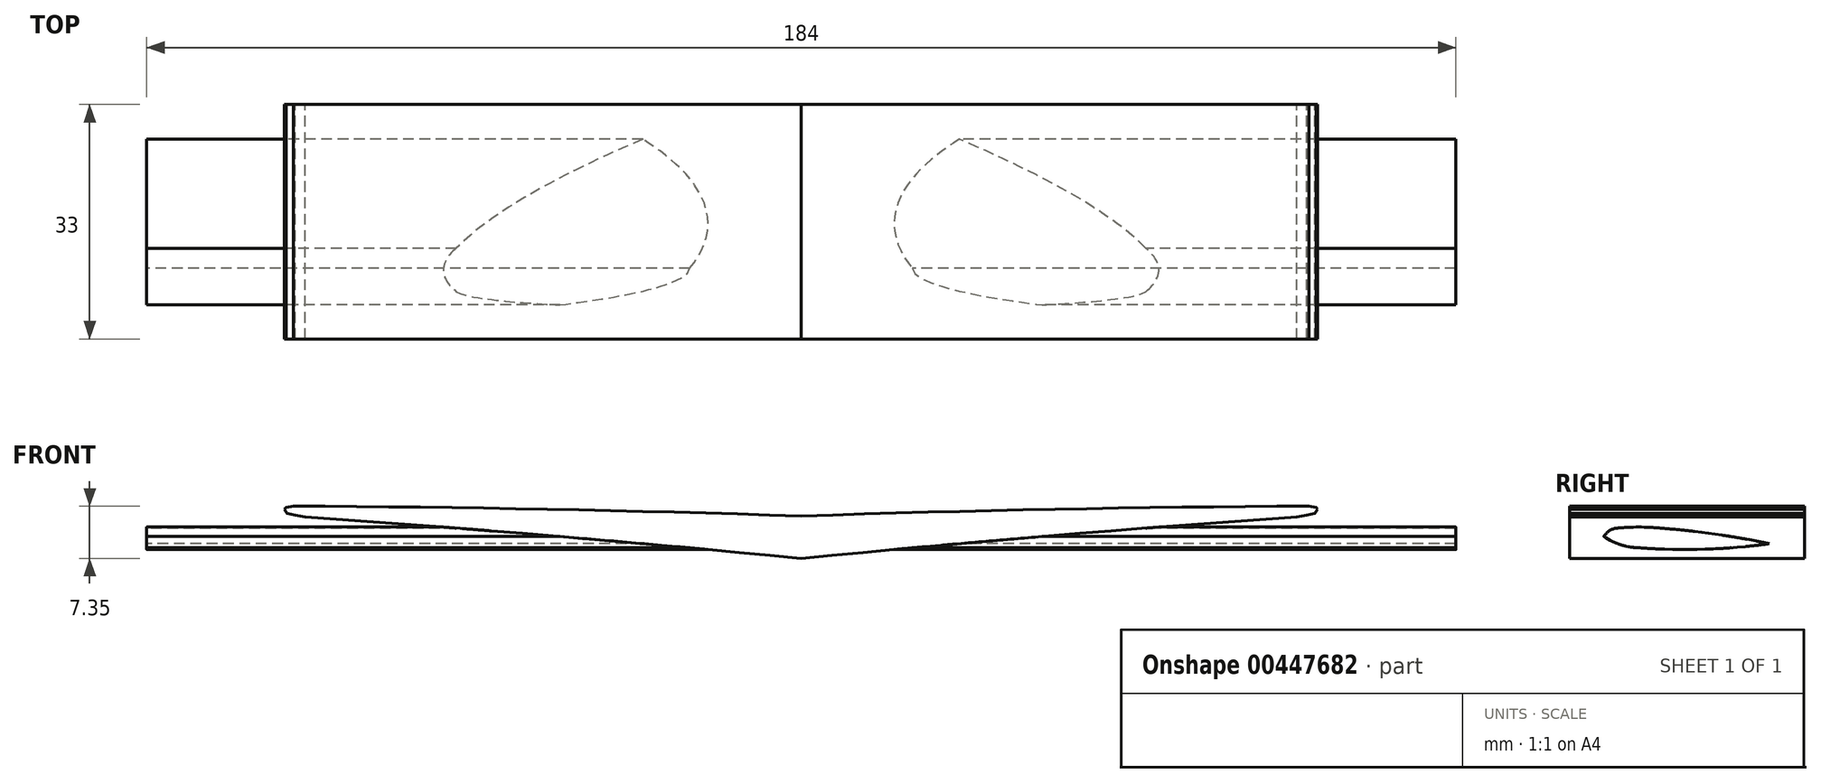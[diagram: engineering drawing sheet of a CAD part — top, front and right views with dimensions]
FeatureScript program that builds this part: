
annotation { "Feature Type Name" : "Feature", "Feature Type Description" : "" }
export const myFeature = defineFeature(function(context is Context, id is Id, definition is map)
    precondition{}
    {
        {
            var Q0;
            Q0=qCreatedBy(makeId("Front.planeOp"),FACE);
            var sketch = newSketch(context, id + "F0", { "sketchPlane" : qUnion([Q0])});
            skArc(sketch, "E0", {"start": v(-0.03, 6.7) * mm, "mid": v(-35.71, 7.64) * mm, "end": v(-71.41, 8.1) * mm});
            skArc(sketch, "E1", {"start": v(-0.03, 0.74) * mm, "mid": v(-34.86, 3.89) * mm, "end": v(-69.73, 6.57) * mm});
            skLineSegment(sketch, "E2", {"start": v(-71.41, 8.1) * mm, "end": v(-72.42, 7.88) * mm});
            skLineSegment(sketch, "E3", {"start": v(-72.42, 7.88) * mm, "end": v(-72.63, 7.63) * mm});
            skLineSegment(sketch, "E4", {"start": v(-72.63, 7.63) * mm, "end": v(-72.26, 7.06) * mm});
            skLineSegment(sketch, "E5", {"start": v(-72.26, 7.06) * mm, "end": v(-71.11, 6.8) * mm});
            skLineSegment(sketch, "E6", {"start": v(-71.11, 6.8) * mm, "end": v(-69.73, 6.57) * mm});
            skLineSegment(sketch, "E7", {"start": v(-0.03, 6.7) * mm, "end": v(-0.03, 0.74) * mm});
            skArc(sketch, "E8.MirrorCS", {"start": v(-0.03, 6.7) * mm, "mid": v(35.66, 7.64) * mm, "end": v(71.36, 8.1) * mm});
            skArc(sketch, "E9.MirrorCS", {"start": v(-0.03, 0.74) * mm, "mid": v(34.8, 3.89) * mm, "end": v(69.68, 6.57) * mm});
            skLineSegment(sketch, "E10.MirrorCS", {"start": v(71.06, 6.8) * mm, "end": v(69.68, 6.57) * mm});
            skLineSegment(sketch, "E11.MirrorCS", {"start": v(72.21, 7.06) * mm, "end": v(71.06, 6.8) * mm});
            skLineSegment(sketch, "E12.MirrorCS", {"start": v(72.58, 7.63) * mm, "end": v(72.21, 7.06) * mm});
            skLineSegment(sketch, "E13.MirrorCS", {"start": v(72.36, 7.88) * mm, "end": v(72.58, 7.63) * mm});
            skLineSegment(sketch, "E14.MirrorCS", {"start": v(71.36, 8.1) * mm, "end": v(72.36, 7.88) * mm});
            skSolve(sketch);
        }
        {
            var Q0;
            Q0=qCreatedBy(makeId("Right.planeOp"),FACE);
            var sketch = newSketch(context, id + "F1", { "sketchPlane" : qUnion([Q0])});
            skArc(sketch, "E15", {"start": v(-11.2, 3.8) * mm, "mid": v(-8.74, 2.63) * mm, "end": v(-6.05, 2.21) * mm});
            skArc(sketch, "E16", {"start": v(-6.05, 2.21) * mm, "mid": v(3.04, 2.02) * mm, "end": v(12.1, 2.8) * mm});
            skArc(sketch, "E17", {"start": v(-9.33, 5) * mm, "mid": v(-10.4, 4.62) * mm, "end": v(-11.2, 3.8) * mm});
            skArc(sketch, "E18", {"start": v(-3.22, 5) * mm, "mid": v(-6.27, 5.13) * mm, "end": v(-9.33, 5) * mm});
            skArc(sketch, "E19", {"start": v(12.1, 2.8) * mm, "mid": v(4.47, 4.14) * mm, "end": v(-3.22, 5) * mm});
            skSolve(sketch);
        }
        {
            var Q0;
            Q0 = qSketchRegion(id + "F0", true);
            extrude(context, id + "F2", {"entities" : qUnion([Q0]), "depth" : 16 * mm, "hasSecondDirection" : true, "secondDirectionOppositeDirection" : true, "secondDirectionDepth" : 17 * mm});
        }
        {
            var Q0;
            Q0 = qSketchRegion(id + "F1", true);
            extrude(context, id + "F3", {"entities" : qUnion([Q0]), "operationType" : NewBodyOperationType.ADD, "depth" : 92 * mm, "hasSecondDirection" : true, "secondDirectionOppositeDirection" : true, "secondDirectionDepth" : 92 * mm});
        }
    });
